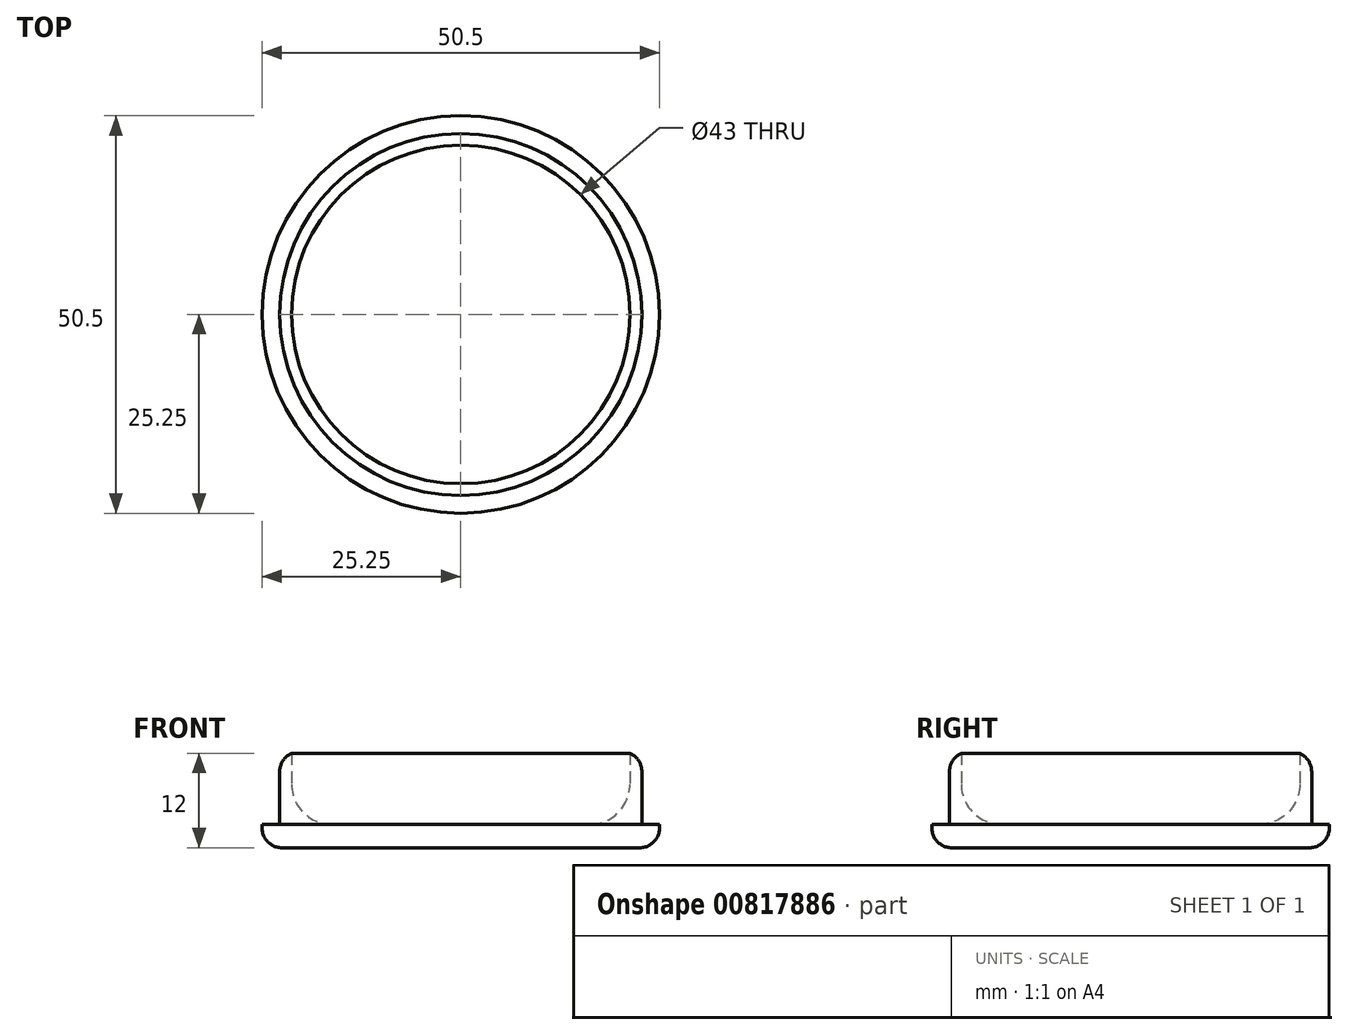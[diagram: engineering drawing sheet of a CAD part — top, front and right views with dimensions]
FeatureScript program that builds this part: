
annotation { "Feature Type Name" : "Feature", "Feature Type Description" : "" }
export const myFeature = defineFeature(function(context is Context, id is Id, definition is map)
    precondition{}
    {
        {
            var Q0;
            Q0=qCreatedBy(makeId("Top.planeOp"),FACE);
            var sketch = newSketch(context, id + "F0", { "sketchPlane" : qUnion([Q0])});
            skCircle(sketch, "E0", {"center": v(0, 0) * mm, "radius": 25.25 * mm});
            skSolve(sketch);
        }
        {
            var Q0;
            Q0 = qSketchRegion(id + "F0", true);
            extrude(context, id + "F1", {"entities" : qUnion([Q0]), "depth" : 3 * mm, "offsetDistance" : 25.4 * mm});
        }
        {
            var Q0;
            Q0=makeQuery(id+"F1.opExtrude","CAP_FACE",FACE,{"disambiguationData":[OSD([sQuery(id+"F0.wireOp",EDGE,"E0")])],"isStart":false});
            var sketch = newSketch(context, id + "F2", { "sketchPlane" : qUnion([Q0])});
            skCircle(sketch, "E1", {"center": v(0, 0) * mm, "radius": 23 * mm});
            skCircle(sketch, "E2", {"center": v(0, 0) * mm, "radius": 21.5 * mm});
            skSolve(sketch);
        }
        {
            var Q0;
            Q0=makeQuery(id+"F2.imprint","IMPRINT",FACE,{"disambiguationData":[TD([[makeQuery(id+"F2.imprint","IMPRINT",EDGE,{"derivedFrom":sQuery(id+"F2.wireOp",EDGE,"E1")}),1.0]])]});
            extrude(context, id + "F3", {"entities" : qUnion([Q0]), "operationType" : NewBodyOperationType.ADD, "depth" : 9 * mm, "offsetDistance" : 25.4 * mm});
        }
        {
            var Q0;
            Q0=makeQuery(id+"F1.opExtrude","CAP_EDGE",EDGE,{"disambiguationData":[OSD([sQuery(id+"F0.wireOp",EDGE,"E0")])],"isStart":true});
            fillet(context, id + "F4", {"entities" : qUnion([Q0]), "tangentPropagation" : true, "radius" : 2.54 * mm, "defaultsChanged" : true, "vertexSettings" : [], "allowEdgeOverflow" : false});
        }
        {
            var Q0;
            Q0=makeQuery(id+"F3.opExtrude","CAP_EDGE",EDGE,{"disambiguationData":[OSD([sQuery(id+"F2.wireOp",EDGE,"E1")])],"isStart":false});
            fillet(context, id + "F5", {"entities" : qUnion([Q0]), "tangentPropagation" : true, "radius" : 2.54 * mm, "defaultsChanged" : true, "vertexSettings" : [], "allowEdgeOverflow" : false});
        }
        {
            var Q0;
            Q0=makeQuery(id+"F3.opExtrude","CAP_EDGE",EDGE,{"disambiguationData":[OSD([sQuery(id+"F2.wireOp",EDGE,"E2")])],"isStart":true});
            fillet(context, id + "F6", {"entities" : qUnion([Q0]), "tangentPropagation" : true, "radius" : 5.08 * mm, "defaultsChanged" : true, "vertexSettings" : [], "allowEdgeOverflow" : false});
        }
    });
